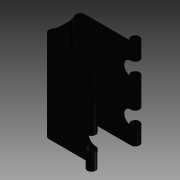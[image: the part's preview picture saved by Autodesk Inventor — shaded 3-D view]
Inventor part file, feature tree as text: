
AUTODESK INVENTOR PART (.ipt)
format: ipt  version: 2013 (Build 170138000, 138)  size: 176,128 bytes
history: native  units: mm
features: sketch x4, extrude x2, sweep x1, mirror x1
ambient origin geometry x8: Origin, YZ Plane, XZ Plane, XY Plane, X Axis, Y Axis, Z Axis, Center Point
bodies: Solid1 (feature_tree)
feature tree (8):
  sweep  "Sweep1"
  extrude  "Extrusion1"  Depth=1.0mm
  extrude  "Extrusion2"  Depth=0.1mm
  mirror  "Mirror1"
  sketch  "Sketch1"  dims[d0=1.5mm d2=17.0mm]
  sketch  "Sketch2"  dims[d3=6.25mm d4=1.0mm]
  sketch  "Sketch3"  dims[d5=5.0mm d6=0.1mm]
  sketch  "Sketch4"  dims[d8=32.0mm d9=0.0mm d10=5.0mm d12=6.0mm d13=0.0mm d14=0.0mm d15=0.0mm d16=0.0mm]
